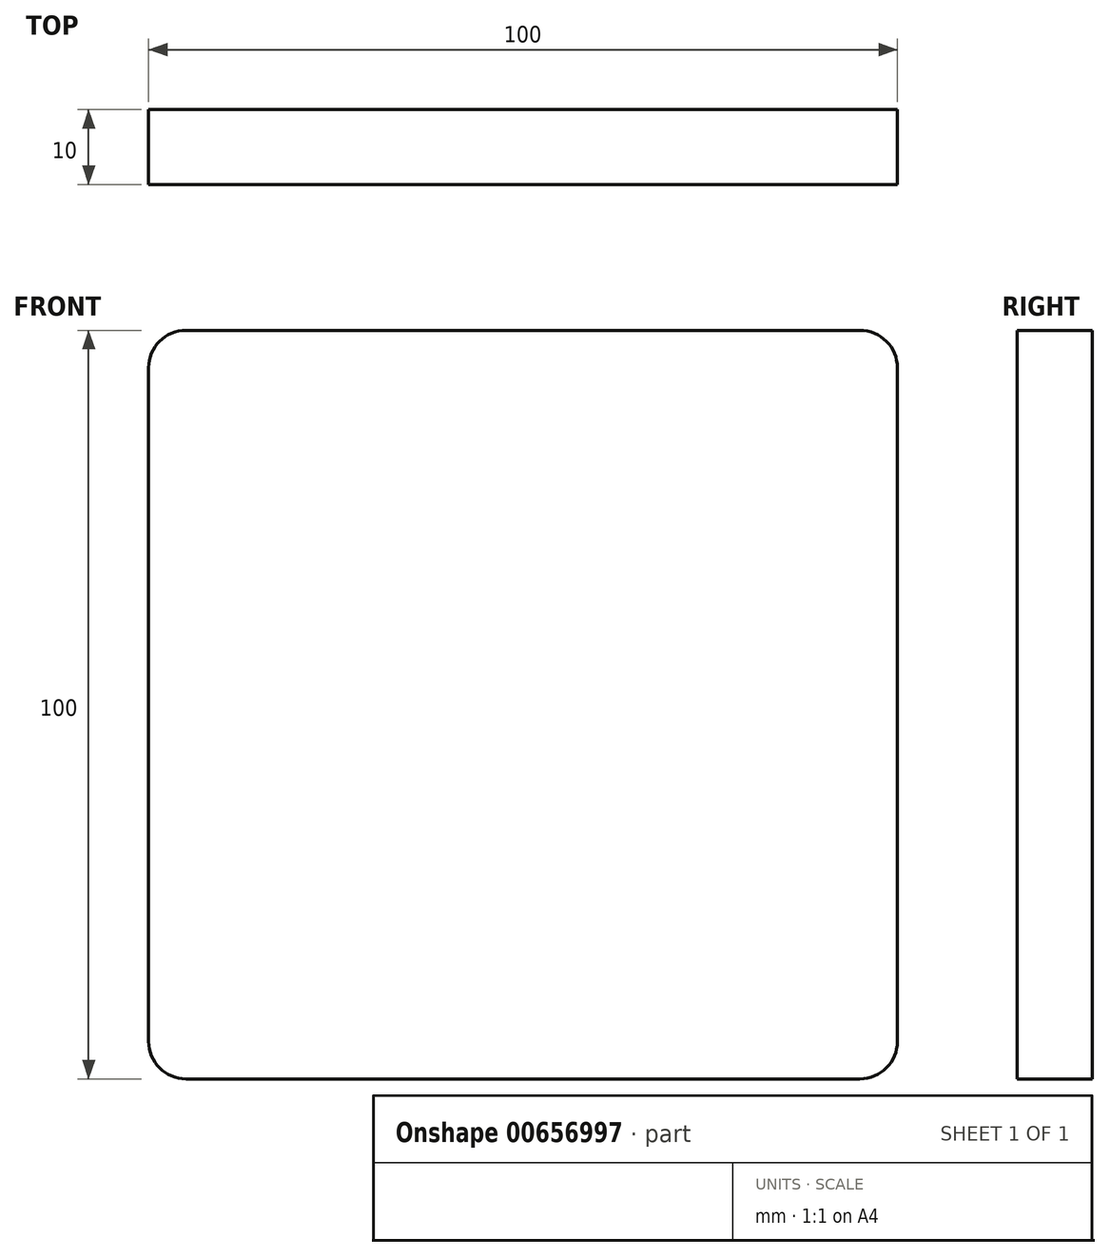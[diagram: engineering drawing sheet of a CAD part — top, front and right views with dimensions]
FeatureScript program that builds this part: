
annotation { "Feature Type Name" : "Feature", "Feature Type Description" : "" }
export const myFeature = defineFeature(function(context is Context, id is Id, definition is map)
    precondition{}
    {
        {
            var Q0;
            Q0=qCreatedBy(makeId("Front.planeOp"),FACE);
            var sketch = newSketch(context, id + "F0", { "sketchPlane" : qUnion([Q0])});
            skLineSegment(sketch, "E0.bottom", {"start": v(-59.86, 32.57) * mm, "end": v(40.14, 32.57) * mm});
            skLineSegment(sketch, "E0.top", {"start": v(-59.86, -67.43) * mm, "end": v(40.14, -67.43) * mm});
            skLineSegment(sketch, "E0.left", {"start": v(-59.86, 32.57) * mm, "end": v(-59.86, -67.43) * mm});
            skLineSegment(sketch, "E0.right", {"start": v(40.14, 32.57) * mm, "end": v(40.14, -67.43) * mm});
            skSolve(sketch);
        }
        {
            var Q0;
            Q0 = qSketchRegion(id + "F0", true);
            var Q1;
            Q1=makeQuery(id+"F0.imprint","IMPRINT",FACE,{"disambiguationData":[TD([[makeQuery(id+"F0.imprint","IMPRINT",EDGE,{"derivedFrom":sQuery(id+"F0.wireOp",EDGE,"E0.bottom")}),-1.0]])]});
            extrude(context, id + "F1", {"entities" : qUnion([Q0, Q1]), "depth" : 10 * mm, "offsetDistance" : 25.4 * mm});
        }
        {
            var Q0;
            Q0=makeQuery(id+"F1.opExtrude","SWEPT_EDGE",EDGE,{"disambiguationData":[OSD([sQuery(id+"F0.wireOp",EDGE,"E0.bottom"),sQuery(id+"F0.wireOp",EDGE,"E0.right")])]});
            var Q1;
            Q1=makeQuery(id+"F1.opExtrude","SWEPT_EDGE",EDGE,{"disambiguationData":[OSD([sQuery(id+"F0.wireOp",EDGE,"E0.bottom"),sQuery(id+"F0.wireOp",EDGE,"E0.left")])]});
            var Q2;
            Q2=makeQuery(id+"F1.opExtrude","SWEPT_EDGE",EDGE,{"disambiguationData":[OSD([sQuery(id+"F0.wireOp",EDGE,"E0.top"),sQuery(id+"F0.wireOp",EDGE,"E0.right")])]});
            var Q3;
            Q3=makeQuery(id+"F1.opExtrude","SWEPT_EDGE",EDGE,{"disambiguationData":[OSD([sQuery(id+"F0.wireOp",EDGE,"E0.top"),sQuery(id+"F0.wireOp",EDGE,"E0.left")])]});
            fillet(context, id + "F2", {"entities" : qUnion([Q0, Q1, Q2, Q3]), "radius" : 5 * mm, "tangentPropagation" : true, "allowEdgeOverflow" : false});
        }
    });
